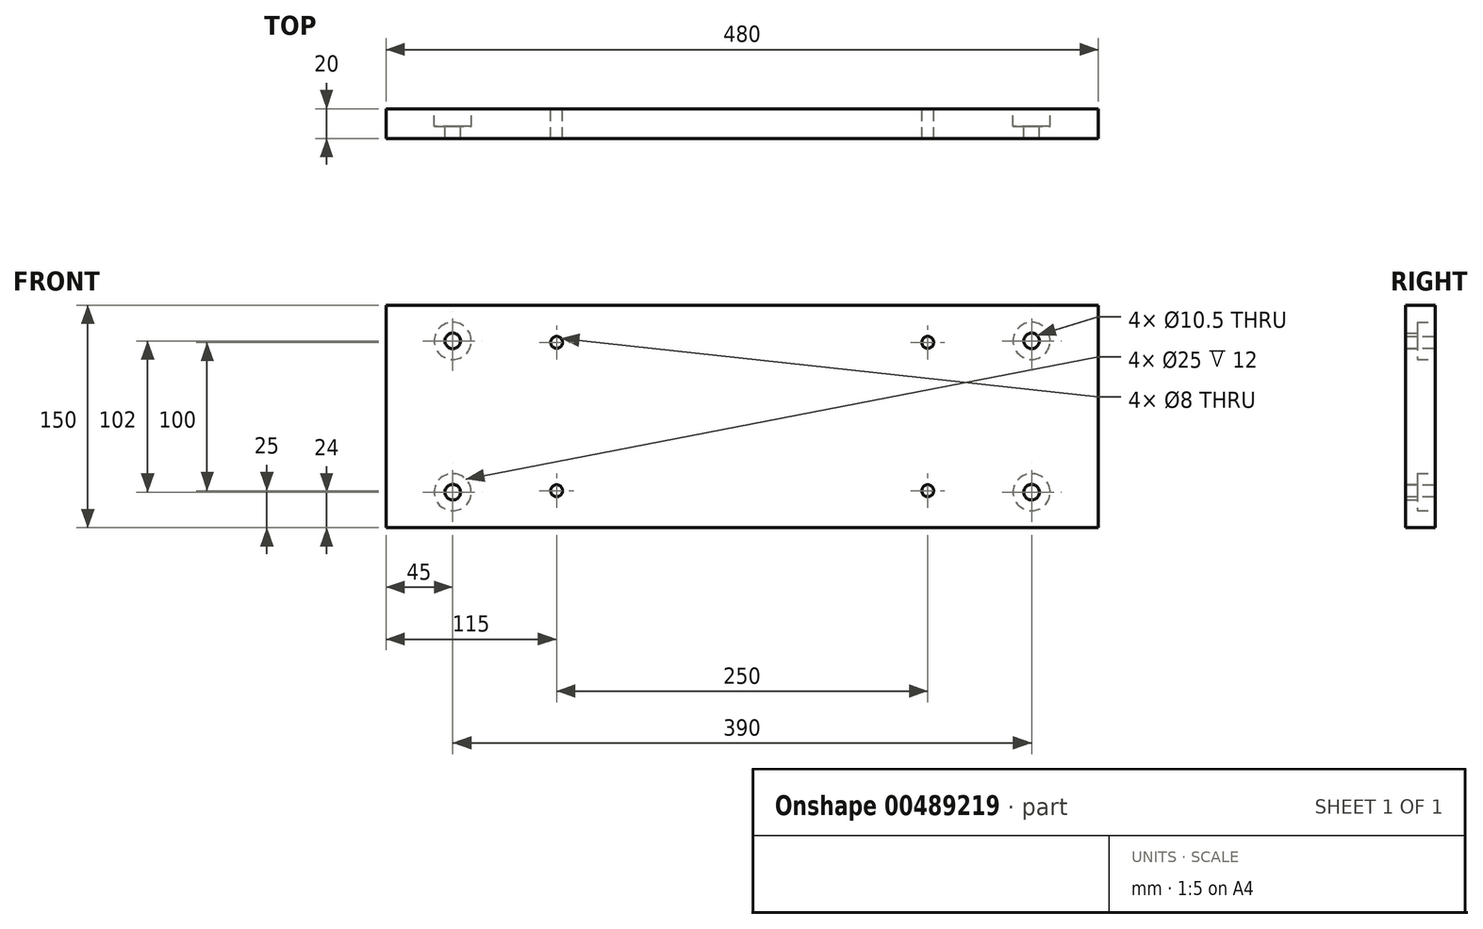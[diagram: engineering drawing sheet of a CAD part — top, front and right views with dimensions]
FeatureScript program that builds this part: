
annotation { "Feature Type Name" : "Feature", "Feature Type Description" : "" }
export const myFeature = defineFeature(function(context is Context, id is Id, definition is map)
    precondition{}
    {
        {
            var Q0;
            Q0=qCreatedBy(makeId("Front.planeOp"),FACE);
            var sketch = newSketch(context, id + "F0", { "sketchPlane" : qUnion([Q0])});
            skLineSegment(sketch, "E0.bottom", {"start": v(0, 0) * mm, "end": v(480, 0) * mm});
            skLineSegment(sketch, "E0.top", {"start": v(0, 150) * mm, "end": v(480, 150) * mm});
            skLineSegment(sketch, "E0.left", {"start": v(0, 0) * mm, "end": v(0, 150) * mm});
            skLineSegment(sketch, "E0.right", {"start": v(480, 0) * mm, "end": v(480, 150) * mm});
            skPoint(sketch, "E1.centerSnap0", {"position": v(480, 75) * mm});
            skPoint(sketch, "E1.centerSnap1", {"position": v(240, 0) * mm});
            skLineSegment(sketch, "E2", {"start": v(240, 75) * mm, "end": v(0, 75) * mm, "construction": true});
            skPoint(sketch, "E3", {"position": v(45, 126) * mm});
            skPoint(sketch, "E4.MirrorP", {"position": v(45, 24) * mm});
            skLineSegment(sketch, "E5", {"start": v(240, 75) * mm, "end": v(240, 182.53) * mm, "construction": true});
            skPoint(sketch, "E5.endSnap0", {"position": v(240, 150) * mm});
            skPoint(sketch, "E6.MirrorP", {"position": v(435, 24) * mm});
            skPoint(sketch, "E7.MirrorP", {"position": v(435, 126) * mm});
            skPoint(sketch, "E8", {"position": v(365, 125) * mm});
            skPoint(sketch, "E9.MirrorP", {"position": v(365, 25) * mm});
            skPoint(sketch, "E10.MirrorP", {"position": v(115, 25) * mm});
            skPoint(sketch, "E11.MirrorP", {"position": v(115, 125) * mm});
            skSolve(sketch);
        }
        {
            var Q0;
            Q0=makeQuery(id+"F0.imprint","IMPRINT",FACE,{"disambiguationData":[TD([[makeQuery(id+"F0.imprint","IMPRINT",EDGE,{"derivedFrom":sQuery(id+"F0.wireOp",EDGE,"E0.bottom")}),1.0]])]});
            extrude(context, id + "F1", {"entities" : qUnion([Q0]), "depth" : 20 * mm, "offsetDistance" : 25 * mm});
        }
        {
            var Q0;
            Q0=sQuery(id+"F0.wireOp",VERTEX,"E7.MirrorP");
            var Q1;
            Q1=sQuery(id+"F0.wireOp",VERTEX,"E6.MirrorP");
            var Q2;
            Q2=sQuery(id+"F0.wireOp",VERTEX,"E3");
            var Q3;
            Q3=sQuery(id+"F0.wireOp",VERTEX,"E4.MirrorP");
            var Q4;
            Q4=makeQuery(id+"F1.opExtrude","SWEPT_BODY",BODY,{"disambiguationData":[OSD([sQuery(id+"F0.wireOp",EDGE,"E0.bottom"),sQuery(id+"F0.wireOp",EDGE,"E0.top"),sQuery(id+"F0.wireOp",EDGE,"E0.left"),sQuery(id+"F0.wireOp",EDGE,"E0.right"),sQuery(id+"F0.wireOp",EDGE,"E1")])]});
            hole(context, id + "F2", {"style" : HoleStyle.C_BORE, "endStyle" : HoleEndStyle.BLIND, "oppositeDirection" : true, "standardTappedOrClearance" : lookupTablePath({ "standard" : "ISO", "size" : "10.5", "type" : "Drilled" }), "standardBlindInLast" : lookupTablePath({ "standard" : "ISO", "size" : "10.5", "type" : "Drilled" }), "holeDiameter" : 10.5 * mm, "cBoreDiameter" : 25 * mm, "cBoreDepth" : 12 * mm, "majorDiameter" : 16 * mm, "holeDepth" : 35 * mm, "isTappedThrough" : true, "tappedDepth" : 25 * mm, "tapClearance" : 5, "startFromSketch" : true, "locations" : qUnion([Q0, Q1, Q2, Q3]), "scope" : qUnion([Q4])});
        }
        {
            var Q0;
            Q0=sQuery(id+"F0.wireOp",VERTEX,"E11.MirrorP");
            var Q1;
            Q1=sQuery(id+"F0.wireOp",VERTEX,"E10.MirrorP");
            var Q2;
            Q2=sQuery(id+"F0.wireOp",VERTEX,"E9.MirrorP");
            var Q3;
            Q3=sQuery(id+"F0.wireOp",VERTEX,"E8");
            var Q4;
            Q4=makeQuery(id+"F1.opExtrude","SWEPT_BODY",BODY,{"disambiguationData":[OSD([sQuery(id+"F0.wireOp",EDGE,"E0.bottom"),sQuery(id+"F0.wireOp",EDGE,"E0.top"),sQuery(id+"F0.wireOp",EDGE,"E0.left"),sQuery(id+"F0.wireOp",EDGE,"E0.right")])]});
            hole(context, id + "F3", {"style" : HoleStyle.SIMPLE, "endStyle" : HoleEndStyle.BLIND, "oppositeDirection" : true, "standardTappedOrClearance" : lookupTablePath({ "standard" : "ISO", "size" : "8", "type" : "Drilled" }), "standardBlindInLast" : lookupTablePath({ "standard" : "ISO", "size" : "8", "type" : "Drilled" }), "holeDiameter" : 8 * mm, "majorDiameter" : 5 * mm, "holeDepth" : 35 * mm, "isTappedThrough" : true, "tappedDepth" : 25 * mm, "tapClearance" : 5, "startFromSketch" : true, "locations" : qUnion([Q0, Q1, Q2, Q3]), "scope" : qUnion([Q4])});
        }
    });
